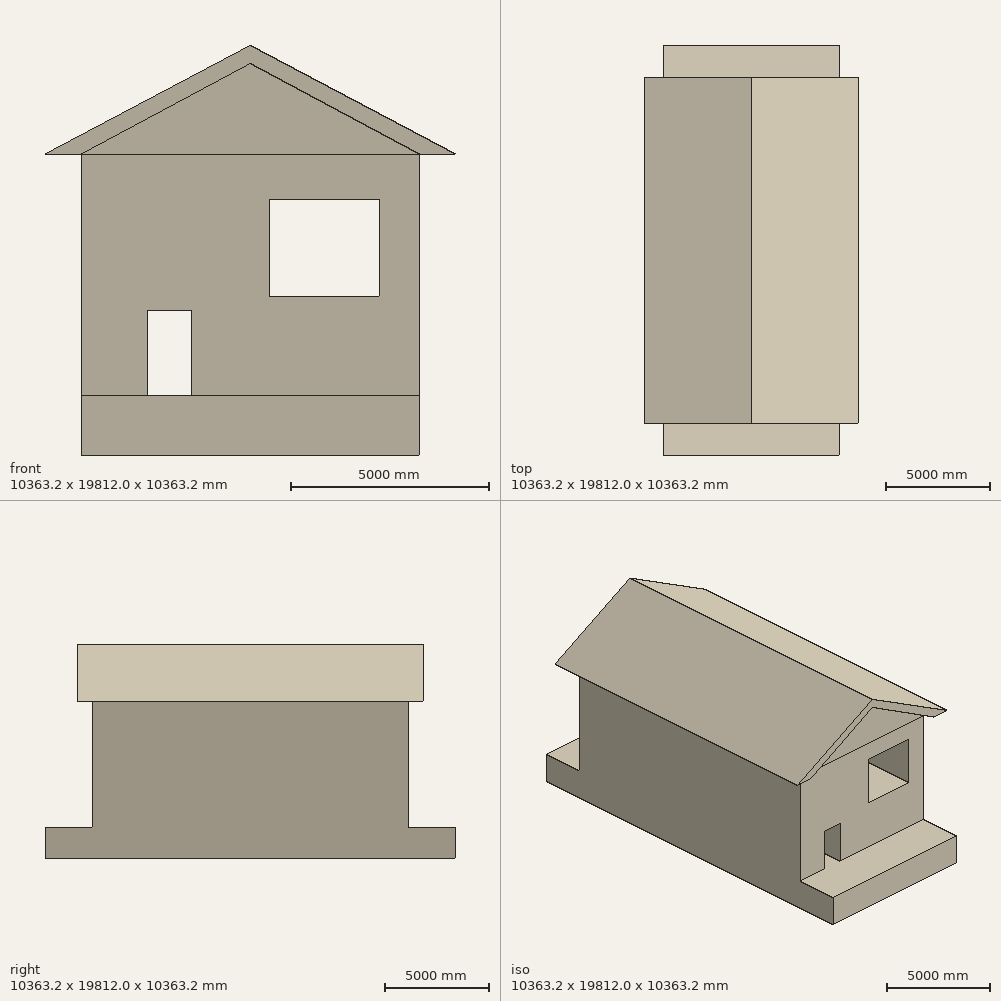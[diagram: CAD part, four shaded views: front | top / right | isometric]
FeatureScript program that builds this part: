
annotation { "Feature Type Name" : "Feature", "Feature Type Description" : "" }
export const myFeature = defineFeature(function(context is Context, id is Id, definition is map)
    precondition{}
    {
        {
            var Q0;
            Q0=qCreatedBy(makeId("Front.planeOp"),FACE);
            var sketch = newSketch(context, id + "F0", { "sketchPlane" : qUnion([Q0])});
            skLineSegment(sketch, "E0", {"start": v(0, 0) * mm, "end": v(4267.2, 0) * mm});
            skLineSegment(sketch, "E1", {"start": v(0, 0) * mm, "end": v(-4267.2, 0) * mm});
            skLineSegment(sketch, "E2", {"start": v(0, 0) * mm, "end": v(0, 2286) * mm});
            skLineSegment(sketch, "E3", {"start": v(0, 2286) * mm, "end": v(4267.2, 0) * mm});
            skLineSegment(sketch, "E4", {"start": v(0, 2286) * mm, "end": v(-4267.2, 0) * mm});
            skLineSegment(sketch, "E5", {"start": v(0, 2286) * mm, "end": v(0, 2743.2) * mm});
            skLineSegment(sketch, "E6", {"start": v(4267.2, 0) * mm, "end": v(5181.6, 0) * mm});
            skLineSegment(sketch, "E7", {"start": v(-4267.2, 0) * mm, "end": v(-5181.6, 0) * mm});
            skLineSegment(sketch, "E8", {"start": v(-5181.6, 0) * mm, "end": v(0, 2743.2) * mm});
            skLineSegment(sketch, "E9", {"start": v(0, 2743.2) * mm, "end": v(5181.6, 0) * mm});
            skLineSegment(sketch, "E10", {"start": v(-4267.2, 0) * mm, "end": v(-4267.2, -6096) * mm});
            skLineSegment(sketch, "E11", {"start": v(4267.2, 0) * mm, "end": v(4267.2, -6096) * mm});
            skLineSegment(sketch, "E12", {"start": v(4267.2, -6096) * mm, "end": v(-4267.2, -6096) * mm});
            skLineSegment(sketch, "E13", {"start": v(-4267.2, -6096) * mm, "end": v(-4267.2, -7620) * mm});
            skLineSegment(sketch, "E14", {"start": v(-4267.2, -7620) * mm, "end": v(4267.2, -7620) * mm});
            skLineSegment(sketch, "E15", {"start": v(4267.2, -7620) * mm, "end": v(4267.2, -6096) * mm});
            skLineSegment(sketch, "E16", {"start": v(-2599.42, -6096) * mm, "end": v(-2599.42, -3962.4) * mm});
            skLineSegment(sketch, "E17", {"start": v(-1500.34, -3962.4) * mm, "end": v(-1500.34, -6096) * mm});
            skLineSegment(sketch, "E18", {"start": v(-1500.34, -6096) * mm, "end": v(-1500.34, -3962.4) * mm});
            skLineSegment(sketch, "E19", {"start": v(-2599.42, -3962.4) * mm, "end": v(-1500.34, -3962.4) * mm});
            skLineSegment(sketch, "E20", {"start": v(484.12, -3599.8) * mm, "end": v(3262.36, -3599.8) * mm});
            skLineSegment(sketch, "E21", {"start": v(3262.36, -3599.8) * mm, "end": v(3262.36, -1161.4) * mm});
            skLineSegment(sketch, "E22", {"start": v(484.12, -3599.8) * mm, "end": v(484.12, -1161.4) * mm});
            skLineSegment(sketch, "E23", {"start": v(484.12, -1161.4) * mm, "end": v(3262.36, -1161.4) * mm});
            skText(sketch, "E24", { "text": "Will", "fontName": "OpenSans-Regular.ttf"});
            const initialGuessF0  = {"E24": [-7.57583, 1.95669, 1, 0, 1.58757]};
            skSetInitialGuess(sketch, initialGuessF0);
            skSolve(sketch);
        }
        {
            var Q0;
            Q0=makeQuery(id+"F0.imprint","IMPRINT",FACE,{"disambiguationData":[TD([[makeQuery(id+"F0.imprint","IMPRINT",EDGE,{"derivedFrom":sQuery(id+"F0.wireOp",EDGE,"E4")}),-1.0]])]});
            var Q1;
            Q1=makeQuery(id+"F0.imprint","IMPRINT",FACE,{"disambiguationData":[TD([[makeQuery(id+"F0.imprint","IMPRINT",EDGE,{"derivedFrom":sQuery(id+"F0.wireOp",EDGE,"E3")}),1.0]])]});
            extrude(context, id + "F1", {"entities" : qUnion([Q0, Q1]), "endBound" : BoundingType.SYMMETRIC, "depth" : 16764 * mm, "offsetDistance" : 30.48 * mm});
        }
        {
            var Q0;
            Q0=makeQuery(id+"F0.imprint","IMPRINT",FACE,{"disambiguationData":[TD([[makeQuery(id+"F0.imprint","IMPRINT",EDGE,{"derivedFrom":sQuery(id+"F0.wireOp",EDGE,"E1")}),-1.0]])]});
            var Q1;
            Q1=makeQuery(id+"F0.imprint","IMPRINT",FACE,{"disambiguationData":[TD([[makeQuery(id+"F0.imprint","IMPRINT",EDGE,{"derivedFrom":sQuery(id+"F0.wireOp",EDGE,"E0")}),1.0]])]});
            extrude(context, id + "F2", {"entities" : qUnion([Q0, Q1]), "operationType" : NewBodyOperationType.ADD, "endBound" : BoundingType.SYMMETRIC, "depth" : 15849.6 * mm, "offsetDistance" : 30.48 * mm});
        }
        {
            var Q0;
            Q0=makeQuery(id+"F0.imprint","IMPRINT",FACE,{"disambiguationData":[TD([[makeQuery(id+"F0.imprint","IMPRINT",EDGE,{"derivedFrom":sQuery(id+"F0.wireOp",EDGE,"E0")}),-1.0]])]});
            extrude(context, id + "F3", {"entities" : qUnion([Q0]), "operationType" : NewBodyOperationType.ADD, "endBound" : BoundingType.SYMMETRIC, "depth" : 15240 * mm, "offsetDistance" : 30.48 * mm});
        }
        {
            var Q0;
            {var subQ0=sQuery(id+"F0.wireOp",EDGE,"E13");Q0=makeQuery(id+"F0.imprint","IMPRINT",FACE,{"disambiguationData":[TD([[makeQuery(id+"F0.imprint","IMPRINT",EDGE,{"derivedFrom":subQ0}),1.0]])]});}
            extrude(context, id + "F4", {"entities" : qUnion([Q0]), "operationType" : NewBodyOperationType.ADD, "endBound" : BoundingType.SYMMETRIC, "depth" : 19812 * mm, "offsetDistance" : 30.48 * mm});
        }
    });
